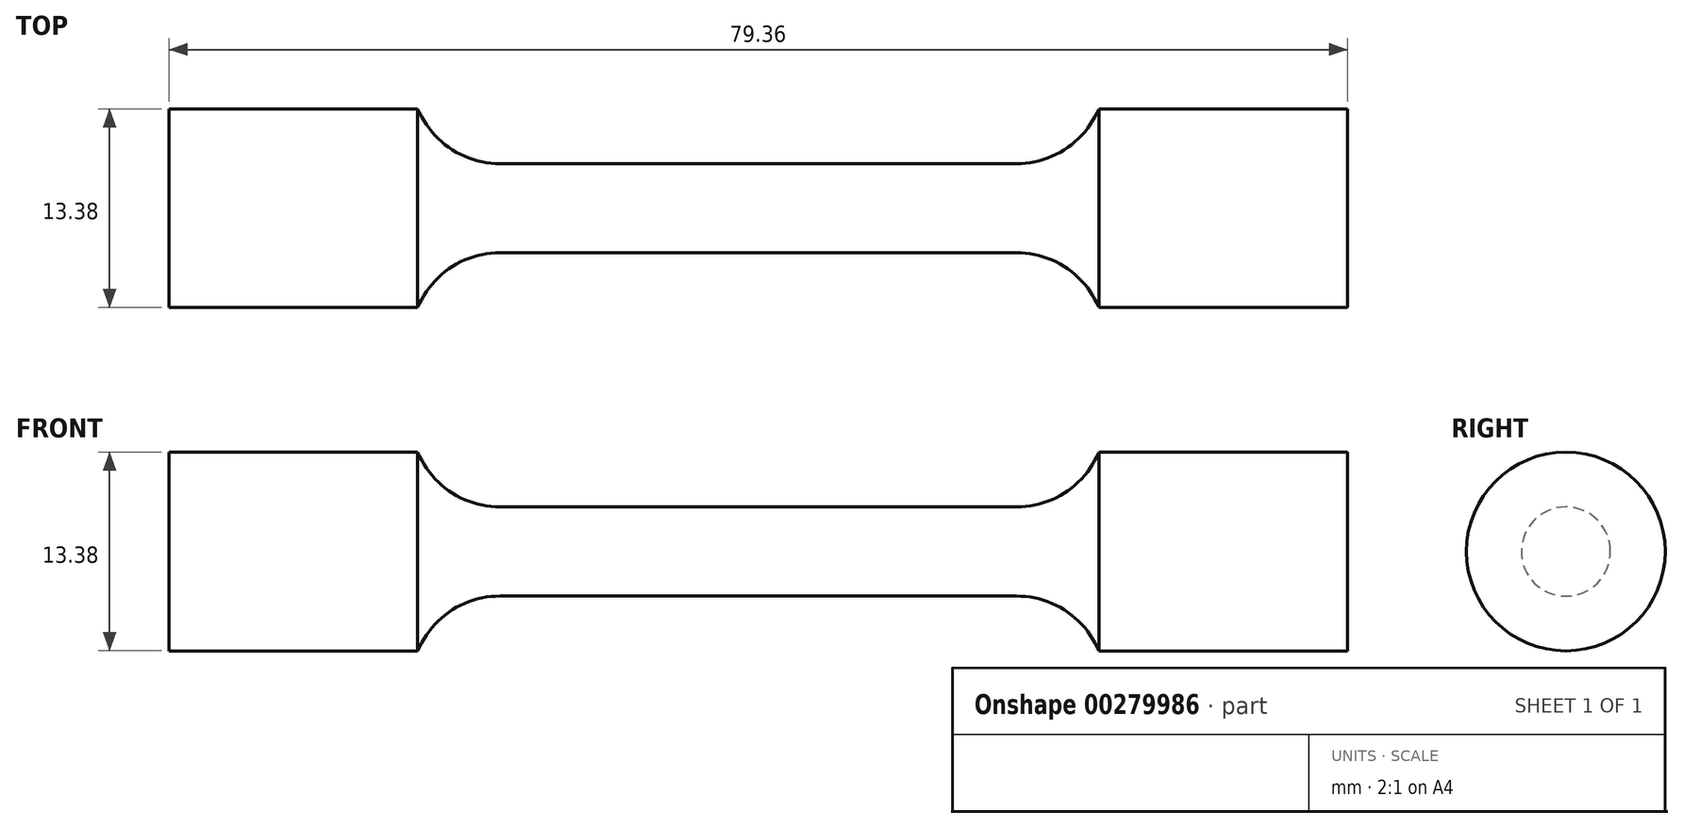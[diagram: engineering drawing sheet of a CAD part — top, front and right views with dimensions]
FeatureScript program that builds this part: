
annotation { "Feature Type Name" : "Feature", "Feature Type Description" : "" }
export const myFeature = defineFeature(function(context is Context, id is Id, definition is map)
    precondition{}
    {
        {
            var Q0;
            Q0=qCreatedBy(makeId("Front.planeOp"),FACE);
            var sketch = newSketch(context, id + "F0", { "sketchPlane" : qUnion([Q0])});
            skLineSegment(sketch, "E0", {"start": v(0, 3) * mm, "end": v(17.39, 3) * mm});
            skArc(sketch, "E1", {"start": v(17.39, 3) * mm, "mid": v(20.72, 4) * mm, "end": v(22.93, 6.7) * mm});
            skLineSegment(sketch, "E2", {"start": v(22.93, 6.7) * mm, "end": v(39.68, 6.7) * mm});
            skLineSegment(sketch, "E3", {"start": v(39.68, 6.7) * mm, "end": v(39.68, 0) * mm});
            skArc(sketch, "E4.MirrorCS", {"start": v(-17.39, 3) * mm, "mid": v(-20.72, 4) * mm, "end": v(-22.93, 6.7) * mm});
            skLineSegment(sketch, "E5.MirrorCS", {"start": v(0, 3) * mm, "end": v(-17.39, 3) * mm});
            skLineSegment(sketch, "E6.MirrorCS", {"start": v(-39.68, 6.7) * mm, "end": v(-39.68, 0) * mm});
            skLineSegment(sketch, "E7.MirrorCS", {"start": v(-22.93, 6.7) * mm, "end": v(-39.68, 6.7) * mm});
            skLineSegment(sketch, "E8", {"start": v(-39.68, 0) * mm, "end": v(39.68, 0) * mm});
            skSolve(sketch);
        }
        {
            var Q0;
            Q0 = qSketchRegion(id + "F0", true);
            var Q1;
            Q1=sQuery(id+"F0.wireOp",EDGE,"E8");
            revolve(context, id + "F1", {"entities" : qUnion([Q0]), "axis" : qUnion([Q1]), "revolveType" : RevolveType.FULL});
        }
    });
